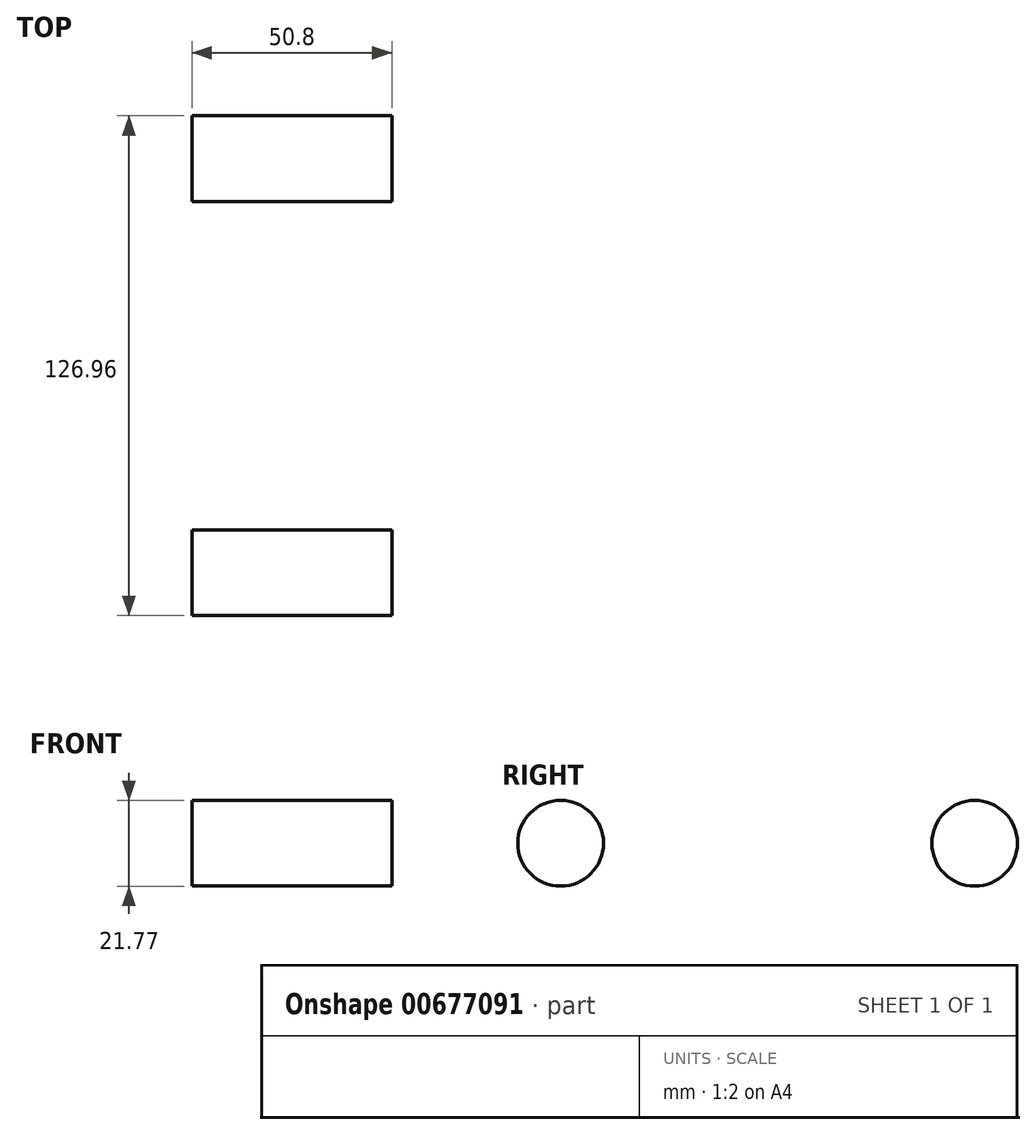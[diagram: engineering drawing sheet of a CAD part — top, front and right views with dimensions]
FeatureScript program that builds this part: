
annotation { "Feature Type Name" : "Feature", "Feature Type Description" : "" }
export const myFeature = defineFeature(function(context is Context, id is Id, definition is map)
    precondition{}
    {
        {
            var Q0;
            Q0=qCreatedBy(makeId("Right.planeOp"),FACE);
            var sketch = newSketch(context, id + "F0", { "sketchPlane" : qUnion([Q0])});
            skCircle(sketch, "E0", {"center": v(-64.34, -22.84) * mm, "radius": 10.88 * mm});
            skCircle(sketch, "E1", {"center": v(40.85, -22.84) * mm, "radius": 10.88 * mm});
            skSolve(sketch);
        }
        {
            var Q0;
            Q0 = qSketchRegion(id + "F0", true);
            extrude(context, id + "F1", {"entities" : qUnion([Q0]), "depth" : 50.8 * mm, "offsetDistance" : 25.4 * mm});
        }
    });
